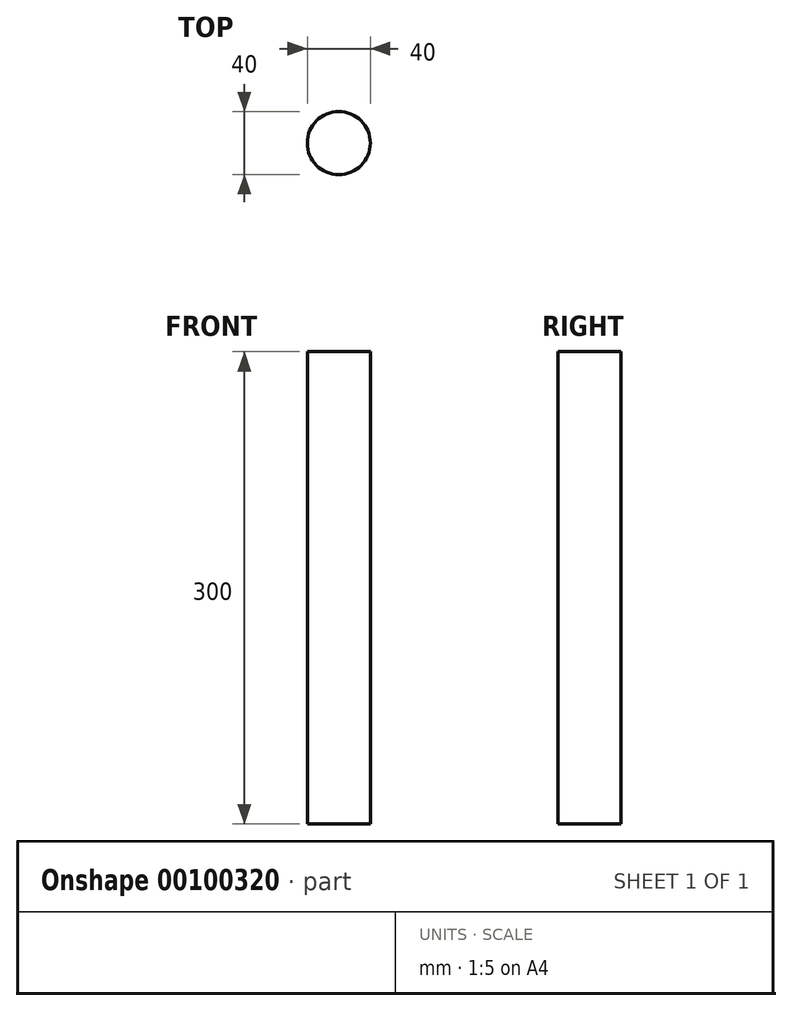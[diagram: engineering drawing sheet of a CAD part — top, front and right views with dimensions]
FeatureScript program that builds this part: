
annotation { "Feature Type Name" : "Feature", "Feature Type Description" : "" }
export const myFeature = defineFeature(function(context is Context, id is Id, definition is map)
    precondition{}
    {
        {
            var Q0;
            Q0=qCreatedBy(makeId("Top.planeOp"),FACE);
            var sketch = newSketch(context, id + "F0", { "sketchPlane" : qUnion([Q0])});
            skCircle(sketch, "E0", {"center": v(0, 0) * mm, "radius": 20 * mm});
            skSolve(sketch);
        }
        {
            var Q0;
            Q0 = qSketchRegion(id + "F0", true);
            extrude(context, id + "F1", {"entities" : qUnion([Q0]), "depth" : 300 * mm});
        }
    });
